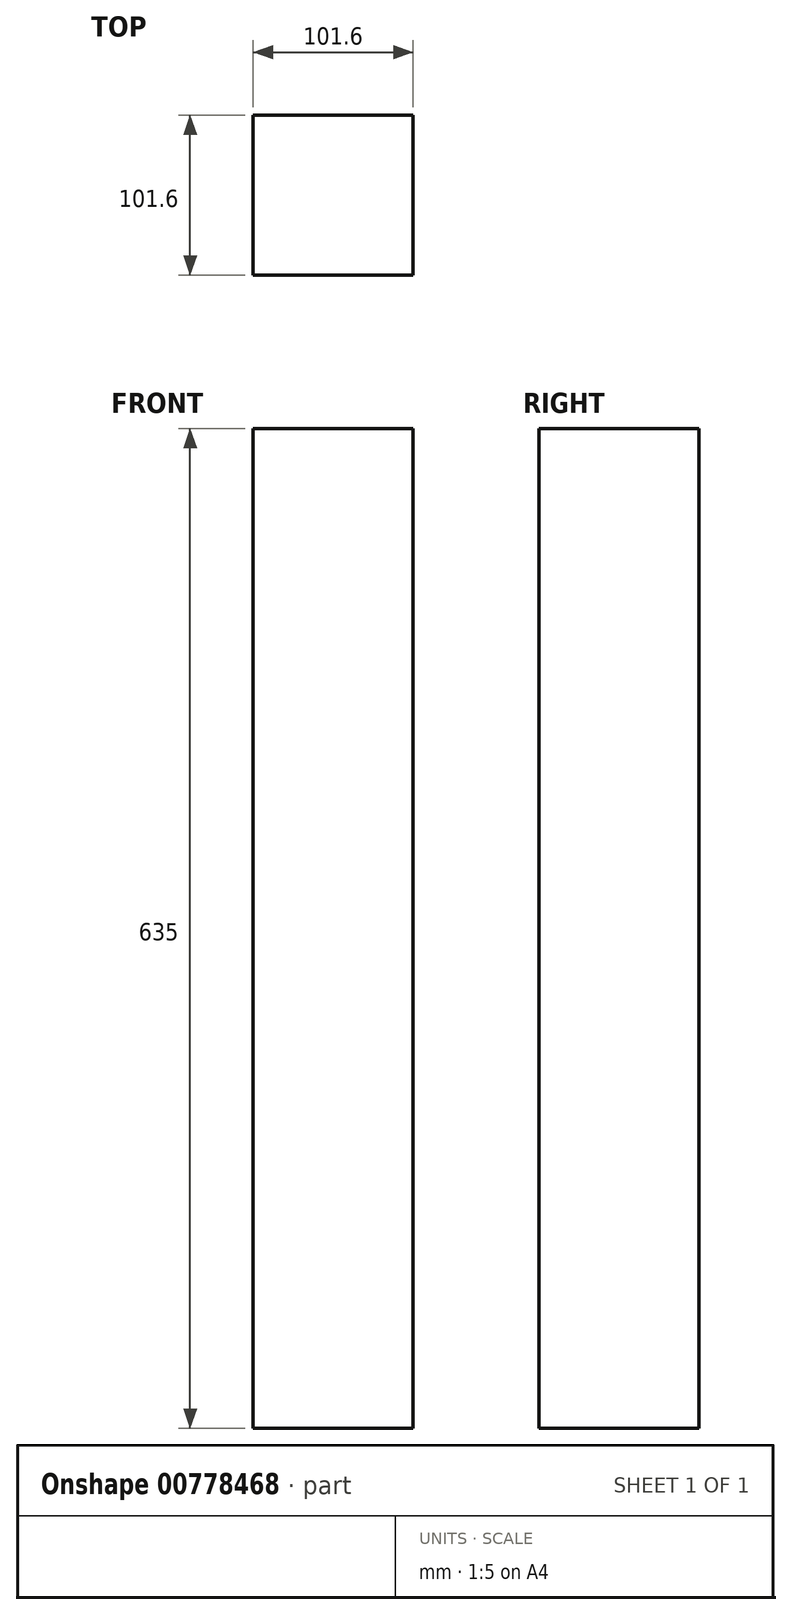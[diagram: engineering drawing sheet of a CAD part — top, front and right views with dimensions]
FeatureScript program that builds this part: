
annotation { "Feature Type Name" : "Feature", "Feature Type Description" : "" }
export const myFeature = defineFeature(function(context is Context, id is Id, definition is map)
    precondition{}
    {
        {
            var Q0;
            Q0=qCreatedBy(makeId("Top.planeOp"),FACE);
            var sketch = newSketch(context, id + "F0", { "sketchPlane" : qUnion([Q0])});
            skLineSegment(sketch, "E0.bottom", {"start": v(-50.8, -50.8) * mm, "end": v(50.8, -50.8) * mm});
            skLineSegment(sketch, "E0.top", {"start": v(-50.8, 50.8) * mm, "end": v(50.8, 50.8) * mm});
            skLineSegment(sketch, "E0.left", {"start": v(-50.8, -50.8) * mm, "end": v(-50.8, 50.8) * mm});
            skLineSegment(sketch, "E0.right", {"start": v(50.8, -50.8) * mm, "end": v(50.8, 50.8) * mm});
            skPoint(sketch, "E0.middle", {"position": v(0, 0) * mm});
            skSolve(sketch);
        }
        {
            var Q0;
            Q0=makeQuery(id+"F0.imprint","IMPRINT",FACE,{"disambiguationData":[TD([[makeQuery(id+"F0.imprint","IMPRINT",EDGE,{"derivedFrom":sQuery(id+"F0.wireOp",EDGE,"E0.bottom")}),1.0]])]});
            extrude(context, id + "F1", {"entities" : qUnion([Q0]), "depth" : 635 * mm, "offsetDistance" : 25.4 * mm});
        }
    });
